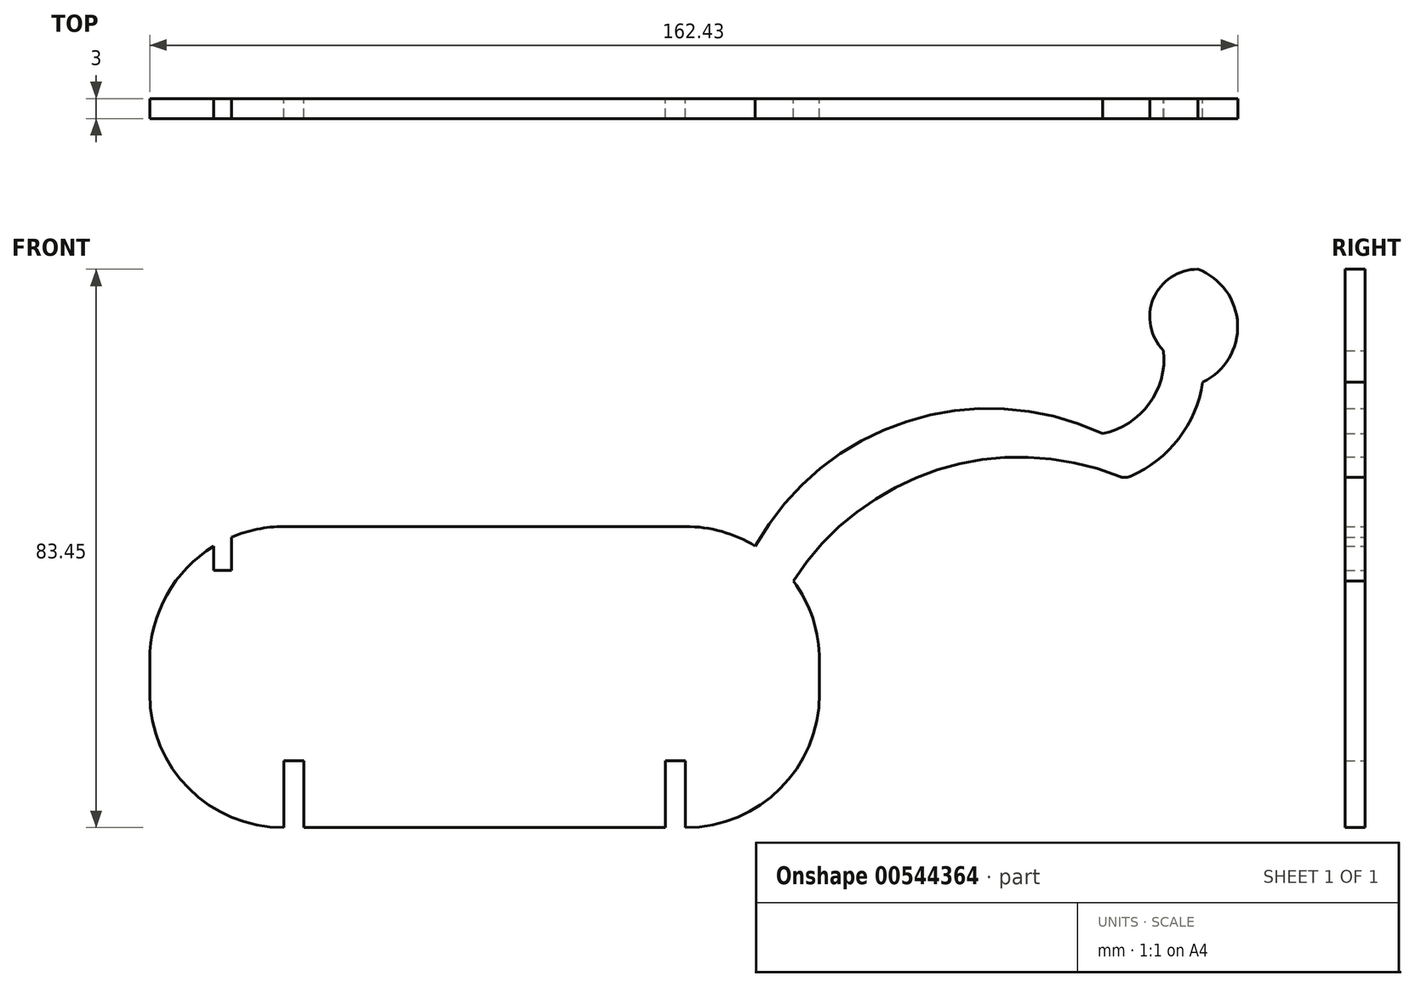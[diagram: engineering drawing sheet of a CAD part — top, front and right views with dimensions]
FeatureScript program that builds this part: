
annotation { "Feature Type Name" : "Feature", "Feature Type Description" : "" }
export const myFeature = defineFeature(function(context is Context, id is Id, definition is map)
    precondition{}
    {
        {
            var Q0;
            Q0=qCreatedBy(makeId("Front.planeOp"),FACE);
            var sketch = newSketch(context, id + "F0", { "sketchPlane" : qUnion([Q0])});
            skLineSegment(sketch, "E0", {"start": v(-32.32, 25.98) * mm, "end": v(27.68, 25.98) * mm});
            skLineSegment(sketch, "E1", {"start": v(-52.32, 5.98) * mm, "end": v(-52.32, 0.98) * mm});
            skLineSegment(sketch, "E2", {"start": v(-29.32, -19.02) * mm, "end": v(24.68, -19.02) * mm});
            skLineSegment(sketch, "E3", {"start": v(47.68, 0.98) * mm, "end": v(47.68, 5.98) * mm});
            skPoint(sketch, "E4.visualSharp", {"position": v(-52.32, 25.98) * mm});
            skArc(sketch, "E4.filletArc", {"start": v(-32.32, 25.98) * mm, "mid": v(-36.3, 25.58) * mm, "end": v(-40.1, 24.4) * mm});
            skPoint(sketch, "E5.visualSharp", {"position": v(-52.32, -19.02) * mm});
            skArc(sketch, "E5.filletArc", {"start": v(-52.32, 0.98) * mm, "mid": v(-46.47, -13.16) * mm, "end": v(-32.32, -19.02) * mm});
            skPoint(sketch, "E6.visualSharp", {"position": v(47.68, 25.98) * mm});
            skArc(sketch, "E6.filletArc", {"start": v(47.68, 5.98) * mm, "mid": v(46.68, 12.22) * mm, "end": v(43.78, 17.84) * mm});
            skPoint(sketch, "E7.visualSharp", {"position": v(47.68, -19.02) * mm});
            skArc(sketch, "E7.filletArc", {"start": v(27.68, -19.02) * mm, "mid": v(41.82, -13.16) * mm, "end": v(47.68, 0.98) * mm});
            skLineSegment(sketch, "E8", {"start": v(-32.32, -19.02) * mm, "end": v(-32.32, -9.02) * mm});
            skLineSegment(sketch, "E9", {"start": v(-32.32, -9.02) * mm, "end": v(-29.32, -9.02) * mm});
            skLineSegment(sketch, "E10", {"start": v(-29.32, -9.02) * mm, "end": v(-29.32, -19.02) * mm});
            skLineSegment(sketch, "E11", {"start": v(27.68, -19.02) * mm, "end": v(27.68, -9.02) * mm});
            skLineSegment(sketch, "E12", {"start": v(27.68, -9.02) * mm, "end": v(24.68, -9.02) * mm});
            skLineSegment(sketch, "E13", {"start": v(24.68, -9.02) * mm, "end": v(24.68, -19.02) * mm});
            skLineSegment(sketch, "E14", {"start": v(-42.77, 23.03) * mm, "end": v(-42.77, 19.4) * mm});
            skLineSegment(sketch, "E15", {"start": v(-42.77, 19.4) * mm, "end": v(-40.1, 19.4) * mm});
            skLineSegment(sketch, "E16", {"start": v(-40.1, 19.4) * mm, "end": v(-40.1, 24.4) * mm});
            skArc(sketch, "E17.trimOffspring", {"start": v(-42.77, 23.03) * mm, "mid": v(-49.77, 15.75) * mm, "end": v(-52.32, 5.98) * mm});
            skArc(sketch, "E18.trimOffspring", {"start": v(38.08, 23.06) * mm, "mid": v(33.08, 25.23) * mm, "end": v(27.68, 25.98) * mm});
            skArc(sketch, "E19", {"start": v(92.5, 33.44) * mm, "mid": v(93.27, 33.3) * mm, "end": v(94.04, 33.46) * mm});
            skArc(sketch, "E20", {"start": v(94.04, 33.46) * mm, "mid": v(101.3, 39.1) * mm, "end": v(104.89, 47.55) * mm});
            skArc(sketch, "E21", {"start": v(104.89, 47.55) * mm, "mid": v(110.1, 56.23) * mm, "end": v(104.14, 64.43) * mm});
            skArc(sketch, "E22", {"start": v(104.14, 64.43) * mm, "mid": v(97.53, 60.04) * mm, "end": v(99.05, 52.26) * mm});
            skArc(sketch, "E23", {"start": v(89.94, 39.87) * mm, "mid": v(96.88, 44.3) * mm, "end": v(99.05, 52.26) * mm});
            skArc(sketch, "E24", {"start": v(89.94, 39.87) * mm, "mid": v(60.7, 41.67) * mm, "end": v(38.08, 23.06) * mm});
            skArc(sketch, "E25", {"start": v(92.5, 33.44) * mm, "mid": v(65.32, 34.45) * mm, "end": v(43.78, 17.84) * mm});
            skPoint(sketch, "E26.visualSharp", {"position": v(136.14, 8.28) * mm});
            skSolve(sketch);
        }
        {
            var Q0;
            Q0=makeQuery(id+"F0.imprint","IMPRINT",FACE,{"disambiguationData":[TD([[makeQuery(id+"F0.imprint","IMPRINT",EDGE,{"derivedFrom":sQuery(id+"F0.wireOp",EDGE,"E0")}),-1.0]])]});
            extrude(context, id + "F1", {"entities" : qUnion([Q0]), "depth" : 3 * mm, "offsetDistance" : 25 * mm});
        }
    });
